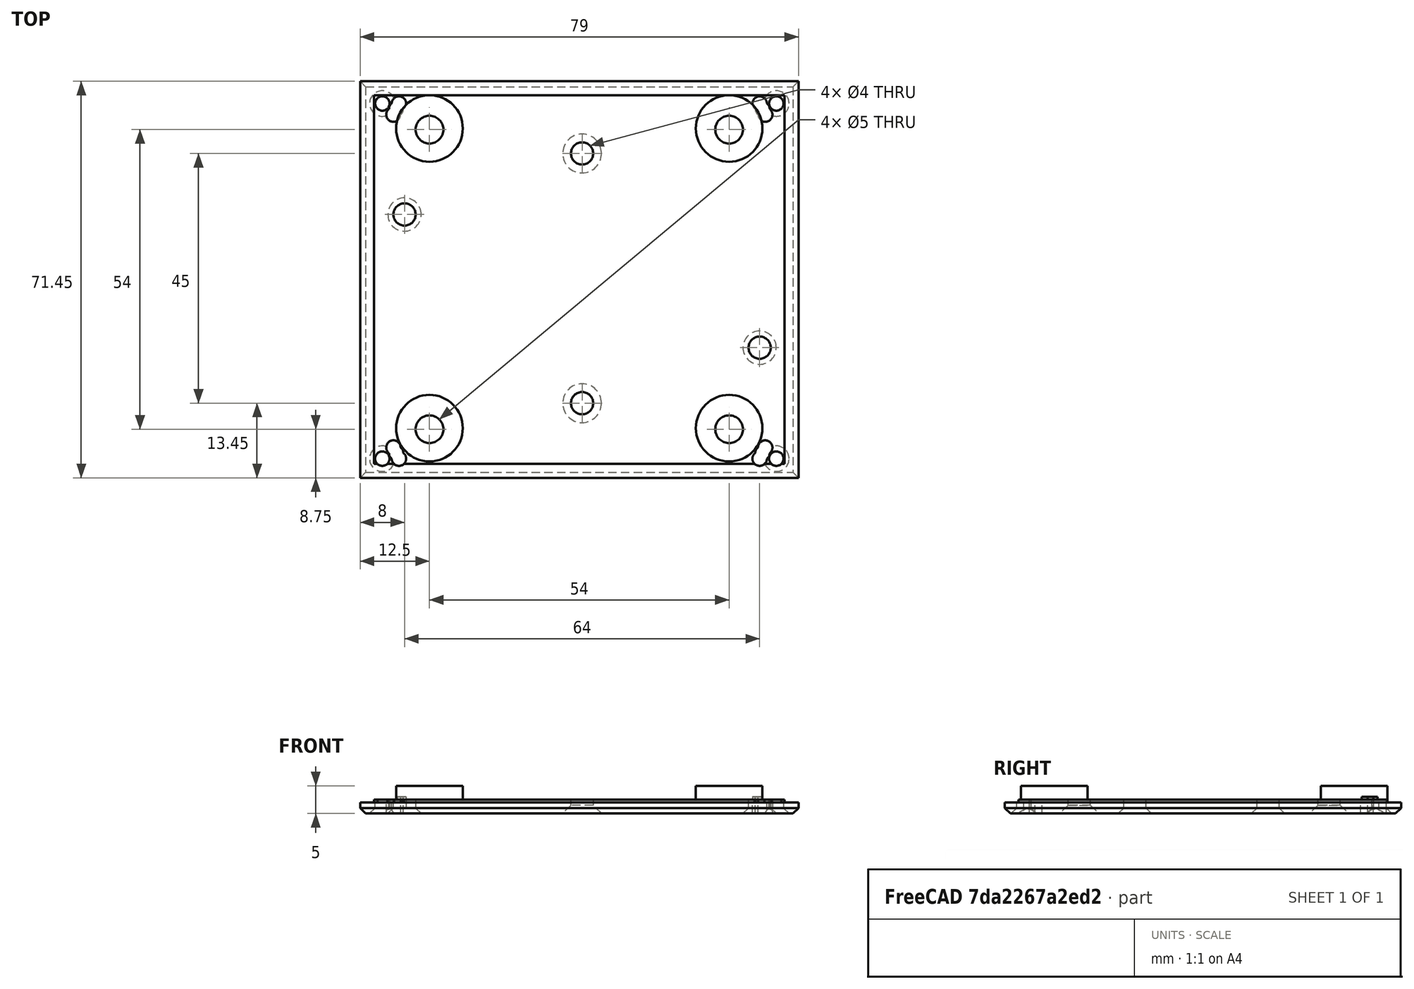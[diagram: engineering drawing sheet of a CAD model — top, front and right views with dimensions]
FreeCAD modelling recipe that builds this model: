
FCSTD DOCUMENT  (FreeCAD 0.20R29177 (Git))
Label: Level crossing top6 n gauge
License: All rights reserved
LicenseURL: http://en.wikipedia.org/wiki/All_rights_reserved
objects: PartDesign::LinearPattern×13, PartDesign::SubtractiveCylinder×8, PartDesign::MultiTransform×6, PartDesign::AdditiveBox×2, PartDesign::Chamfer×2, PartDesign::AdditiveCylinder×1, PartDesign::Body×1
note: 46 computed .brp shape members not serialized (recipe doc carries the construction recipe); baked Part::Feature solids carry a one-line shape summary decoded from their .brp

FEATURE [PartDesign::AdditiveBox] Box
  AttacherType = Attacher::AttachEngine3D
  Height = 2
  Length = 79
  Width = 71.45
FEATURE [PartDesign::LinearPattern] LinearPattern
  Direction = -> X_Axis
  Length = 54
  Occurrences = 2
  Placement = pos=(12.5,8.7,-3) rot=(0,0,1;0rad)
FEATURE [PartDesign::LinearPattern] LinearPattern001
  Direction = -> Y_Axis
  Length = 54
  Occurrences = 2
  Placement = pos=(12.5,8.7,-3) rot=(0,0,1;0rad)
FEATURE [PartDesign::LinearPattern] LinearPattern002
  Direction = -> X_Axis
  Length = 71
  Occurrences = 2
  Placement = pos=(4,4,-1) rot=(0,0,1;0rad)
FEATURE [PartDesign::LinearPattern] LinearPattern003
  Direction = -> Y_Axis
  Length = 64
  Occurrences = 2
  Placement = pos=(4,4,-1) rot=(0,0,1;0rad)
FEATURE [PartDesign::AdditiveBox] Box002
  AttacherType = Attacher::AttachEngine3D
  AttachmentOffset = pos=(2.5,2.5,-0.5) rot=(0,0,1;0rad)
  BaseFeature = -> Box
  Height = 0.5
  Length = 74
  MapMode = 5
  Placement = pos=(2.5,2.5,-0.5) rot=(0,0,1;0rad)
  Support = -> [XY_Plane]
  Width = 66.45
FEATURE [PartDesign::AdditiveCylinder] Cylinder002
  Angle = 360
  AttacherType = Attacher::AttachEngine3D
  AttachmentOffset = pos=(12.5,8.5,-3) rot=(0,0,1;0rad)
  BaseFeature = -> Box002
  FirstAngle = 0
  Height = 5
  MapMode = 5
  Placement = pos=(12.5,8.5,-3) rot=(0,0,1;0rad)
  Radius = 6
  SecondAngle = 0
  Support = -> [XY_Plane]
FEATURE [PartDesign::LinearPattern] LinearPattern004
  Direction = -> X_Axis
  Length = 54
  Occurrences = 2
  Placement = pos=(12.5,8.5,-3) rot=(0,0,1;0rad)
FEATURE [PartDesign::LinearPattern] LinearPattern005
  Direction = -> Y_Axis
  Length = 54
  Occurrences = 2
  Placement = pos=(12.5,8.5,-3) rot=(0,0,1;0rad)
FEATURE [PartDesign::MultiTransform] MultiTransform002
  BaseFeature = -> Cylinder002
  Originals = -> [Cylinder002]
  Placement = pos=(12.5,8.5,-3) rot=(0,0,1;0rad)
  Transformations = -> [LinearPattern004,LinearPattern005]
FEATURE [PartDesign::SubtractiveCylinder] Cylinder
  Angle = 360
  AttacherType = Attacher::AttachEngine3D
  AttachmentOffset = pos=(12.5,8.7,-3) rot=(0,0,1;0rad)
  BaseFeature = -> MultiTransform002
  FirstAngle = 0
  Height = 7
  MapMode = 5
  Placement = pos=(12.5,8.7,-3) rot=(0,0,1;0rad)
  Radius = 2.5
  SecondAngle = 0
  Support = -> [XY_Plane]
FEATURE [PartDesign::MultiTransform] MultiTransform
  BaseFeature = -> Cylinder
  Originals = -> [Cylinder]
  Placement = pos=(12.5,8.7,-3) rot=(0,0,1;0rad)
  Transformations = -> [LinearPattern,LinearPattern001]
FEATURE [PartDesign::SubtractiveCylinder] Cylinder001
  Angle = 360
  AttacherType = Attacher::AttachEngine3D
  AttachmentOffset = pos=(4,4,-1) rot=(0,0,1;0rad)
  BaseFeature = -> MultiTransform
  FirstAngle = 0
  Height = 3
  MapMode = 5
  Placement = pos=(4,4,-1) rot=(0,0,1;0rad)
  Radius = 1.3
  SecondAngle = 0
  Support = -> [XY_Plane]
FEATURE [PartDesign::MultiTransform] MultiTransform001
  BaseFeature = -> Cylinder001
  Originals = -> [Cylinder001]
  Placement = pos=(4,4,-1) rot=(0,0,1;0rad)
  Transformations = -> [LinearPattern002,LinearPattern003]
FEATURE [PartDesign::SubtractiveCylinder] Cylinder003
  Angle = 360
  AttacherType = Attacher::AttachEngine3D
  AttachmentOffset = pos=(8,24,-1) rot=(0,0,1;0rad)
  BaseFeature = -> MultiTransform001
  FirstAngle = 0
  Height = 4
  MapMode = 5
  Placement = pos=(8,24,-1) rot=(0,0,1;0rad)
  Radius = 2
  SecondAngle = 0
  Support = -> [XY_Plane]
FEATURE [PartDesign::SubtractiveCylinder] Cylinder004
  Angle = 360
  AttacherType = Attacher::AttachEngine3D
  AttachmentOffset = pos=(72,48,-2) rot=(0,0,1;0rad)
  BaseFeature = -> Cylinder003
  FirstAngle = 0
  Height = 10
  MapMode = 5
  Placement = pos=(72,48,-2) rot=(0,0,1;0rad)
  Radius = 2
  SecondAngle = 0
  Support = -> [XY_Plane]
FEATURE [PartDesign::Chamfer] Chamfer
  Angle = 45
  Base = -> Cylinder004 [Face3]
  BaseFeature = -> Cylinder004
  ChamferType = 0
  FlipDirection = false
  Placement = pos=(72,48,-2) rot=(0,0,1;0rad)
  Size = 1
  Size2 = 1
  SupportTransform = false
  UseAllEdges = false
FEATURE [PartDesign::SubtractiveCylinder] Cylinder005
  Angle = 360
  AttacherType = Attacher::AttachEngine3D
  AttachmentOffset = pos=(7,4,-1) rot=(0,0,1;0rad)
  BaseFeature = -> Chamfer
  FirstAngle = 0
  Height = 10
  MapMode = 5
  Placement = pos=(7,4,-1) rot=(0,0,1;0rad)
  Radius = 1.3
  SecondAngle = 0
  Support = -> [XY_Plane]
FEATURE [PartDesign::LinearPattern] LinearPattern006
  Direction = -> Y_Axis
  Length = 64
  Occurrences = 2
  Placement = pos=(7,4,-1) rot=(0,0,1;0rad)
FEATURE [PartDesign::LinearPattern] LinearPattern007
  Direction = -> X_Axis
  Length = 65
  Occurrences = 2
  Placement = pos=(7,4,-1) rot=(0,0,1;0rad)
FEATURE [PartDesign::MultiTransform] MultiTransform003
  BaseFeature = -> Cylinder005
  Originals = -> [Cylinder005]
  Placement = pos=(7,4,-1) rot=(0,0,1;0rad)
  Transformations = -> [LinearPattern006,LinearPattern007]
FEATURE [PartDesign::SubtractiveCylinder] Cylinder006
  Angle = 360
  AttacherType = Attacher::AttachEngine3D
  AttachmentOffset = pos=(6,6,-1) rot=(0,0,1;0rad)
  BaseFeature = -> MultiTransform003
  FirstAngle = 0
  Height = 4
  MapMode = 5
  Placement = pos=(6,6,-1) rot=(0,0,1;0rad)
  Radius = 1.3
  SecondAngle = 0
  Support = -> [XY_Plane]
FEATURE [PartDesign::SubtractiveCylinder] Cylinder007
  Angle = 360
  AttacherType = Attacher::AttachEngine3D
  AttachmentOffset = pos=(6.5,5,-1) rot=(0,0,1;0rad)
  BaseFeature = -> Cylinder006
  FirstAngle = 0
  Height = 4
  MapMode = 5
  Placement = pos=(6.5,5,-1) rot=(0,0,1;0rad)
  Radius = 1.3
  SecondAngle = 0
  Support = -> [XY_Plane]
FEATURE [PartDesign::LinearPattern] LinearPattern008
  Direction = -> X_Axis
  Length = 67
  Occurrences = 2
  Placement = pos=(6.5,5,-1) rot=(0,0,1;0rad)
FEATURE [PartDesign::LinearPattern] LinearPattern009
  Direction = -> Y_Axis
  Length = 60
  Occurrences = 2
  Placement = pos=(6.5,5,-1) rot=(0,0,1;0rad)
FEATURE [PartDesign::MultiTransform] MultiTransform004
  BaseFeature = -> Cylinder007
  Originals = -> [Cylinder006]
  Placement = pos=(6.5,5,-1) rot=(0,0,1;0rad)
  Transformations = -> [LinearPattern008,LinearPattern009]
FEATURE [PartDesign::LinearPattern] LinearPattern010
  Direction = -> X_Axis
  Length = 66
  Occurrences = 2
  Placement = pos=(6.5,5,-1) rot=(0,0,1;0rad)
FEATURE [PartDesign::LinearPattern] LinearPattern011
  Direction = -> Y_Axis
  Length = 62
  Occurrences = 2
  Placement = pos=(6.5,5,-1) rot=(0,0,1;0rad)
FEATURE [PartDesign::MultiTransform] MultiTransform005
  BaseFeature = -> MultiTransform004
  Originals = -> [Cylinder007]
  Placement = pos=(6.5,5,-1) rot=(0,0,1;0rad)
  Transformations = -> [LinearPattern010,LinearPattern011]
FEATURE [PartDesign::SubtractiveCylinder] Cylinder008
  Angle = 360
  AttacherType = Attacher::AttachEngine3D
  AttachmentOffset = pos=(40,13,-1) rot=(0,0,1;0rad)
  BaseFeature = -> MultiTransform005
  FirstAngle = 0
  Height = 4
  MapMode = 5
  Placement = pos=(40,13,-1) rot=(0,0,1;0rad)
  Radius = 2
  SecondAngle = 0
  Support = -> [XY_Plane]
FEATURE [PartDesign::LinearPattern] LinearPattern012
  BaseFeature = -> Cylinder008
  Direction = -> Y_Axis
  Length = 45
  Occurrences = 2
  Originals = -> [Cylinder008]
  Placement = pos=(40,13,-1) rot=(0,0,1;0rad)
FEATURE [PartDesign::Chamfer] Chamfer001
  Angle = 45
  Base = -> LinearPattern012 [Edge41,Edge55]
  BaseFeature = -> LinearPattern012
  ChamferType = 0
  FlipDirection = false
  Placement = pos=(40,13,-1) rot=(0,0,1;0rad)
  Size = 1.5
  Size2 = 1
  SupportTransform = false
  UseAllEdges = false
FEATURE [PartDesign::Body] Body
  Group = -> [Box,Box002,Cylinder002,MultiTransform002,Cylinder,MultiTransform,LinearPattern,LinearPattern001,Cylinder001,MultiTransform001,LinearPattern002,LinearPattern003,LinearPattern004,LinearPattern005,Cylinder003,Cylinder004,Chamfer,Cylinder005,MultiTransform003,LinearPattern006,LinearPattern007,Cylinder006,Cylinder007,MultiTransform004,LinearPattern008,LinearPattern009,MultiTransform005,+5 more]
  Origin = -> Origin
  Placement = pos=(0,0,0) rot=(1,0,0;3.14159rad)
  Tip = -> Chamfer001
